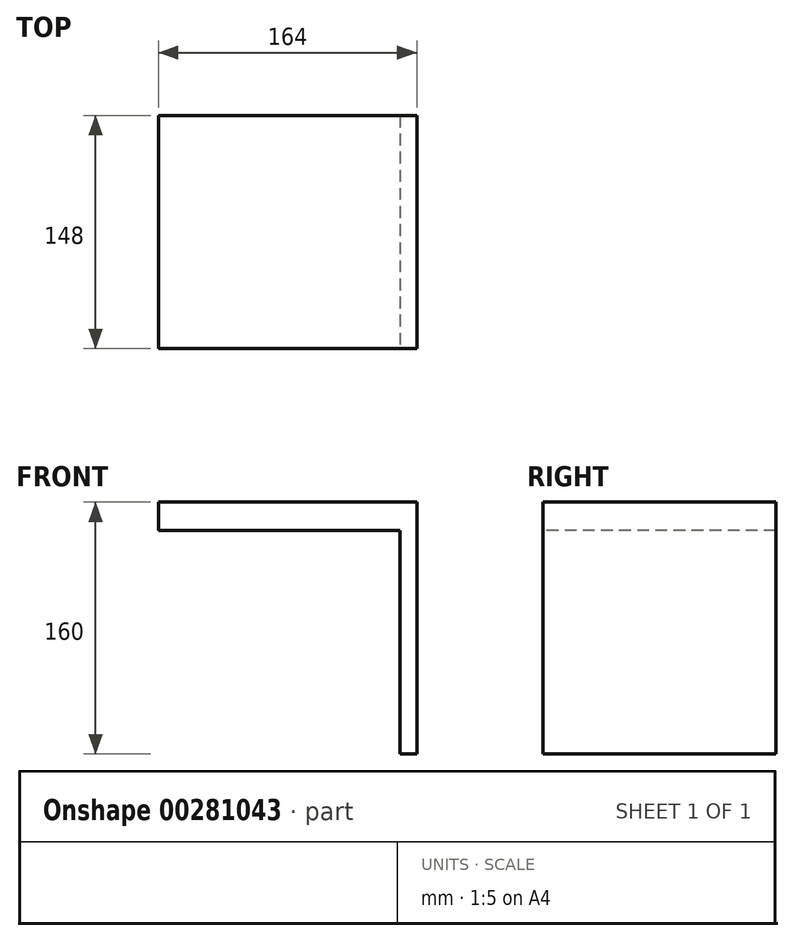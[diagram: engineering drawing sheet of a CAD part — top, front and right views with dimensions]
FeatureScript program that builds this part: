
annotation { "Feature Type Name" : "Feature", "Feature Type Description" : "" }
export const myFeature = defineFeature(function(context is Context, id is Id, definition is map)
    precondition{}
    {
        {
            var Q0;
            Q0=qCreatedBy(makeId("Front.planeOp"),FACE);
            var sketch = newSketch(context, id + "F0", { "sketchPlane" : qUnion([Q0])});
            skLineSegment(sketch, "E0.bottom", {"start": v(-41.99, 130) * mm, "end": v(135.01, 130) * mm});
            skLineSegment(sketch, "E0.top", {"start": v(-41.99, -47) * mm, "end": v(135.01, -47) * mm});
            skLineSegment(sketch, "E0.left", {"start": v(-41.99, 130) * mm, "end": v(-41.99, -47) * mm});
            skLineSegment(sketch, "E0.right", {"start": v(135.01, 130) * mm, "end": v(135.01, -47) * mm});
            skLineSegment(sketch, "E1.bottom", {"start": v(-29.69, 65.72) * mm, "end": v(134.31, 65.72) * mm});
            skLineSegment(sketch, "E1.top", {"start": v(-29.69, -23.24) * mm, "end": v(134.31, -23.24) * mm});
            skLineSegment(sketch, "E1.left", {"start": v(-29.69, 65.72) * mm, "end": v(-29.69, -23.24) * mm});
            skLineSegment(sketch, "E1.right", {"start": v(134.31, 65.72) * mm, "end": v(134.31, -23.24) * mm});
            skLineSegment(sketch, "E2.bottom", {"start": v(-18.19, 148.02) * mm, "end": v(145.81, 148.02) * mm});
            skLineSegment(sketch, "E2.top", {"start": v(-18.19, -11.98) * mm, "end": v(145.81, -11.98) * mm});
            skLineSegment(sketch, "E2.left", {"start": v(-18.19, 148.02) * mm, "end": v(-18.19, -11.98) * mm});
            skLineSegment(sketch, "E2.right", {"start": v(145.81, 148.02) * mm, "end": v(145.81, -11.98) * mm});
            skLineSegment(sketch, "E3", {"start": v(-41.99, 130) * mm, "end": v(-29.69, 65.72) * mm});
            skLineSegment(sketch, "E4", {"start": v(135.01, 130) * mm, "end": v(134.31, 65.72) * mm});
            skLineSegment(sketch, "E5", {"start": v(-41.99, -47) * mm, "end": v(-29.69, -23.24) * mm});
            skLineSegment(sketch, "E6", {"start": v(135.01, -47) * mm, "end": v(134.31, -23.24) * mm});
            skLineSegment(sketch, "E7", {"start": v(145.81, -11.98) * mm, "end": v(134.31, -23.24) * mm});
            skLineSegment(sketch, "E8", {"start": v(134.31, 65.72) * mm, "end": v(145.81, 148.02) * mm});
            skLineSegment(sketch, "E9", {"start": v(-29.69, 65.72) * mm, "end": v(-18.19, 148.02) * mm});
            skLineSegment(sketch, "E10", {"start": v(-29.69, -23.24) * mm, "end": v(-18.19, -11.98) * mm});
            skSolve(sketch);
        }
        {
            var Q0;
            {var subQ5=sQuery(id+"F0.wireOp",EDGE,"E2.right");Q0=makeQuery(id+"F0.imprint","IMPRINT",FACE,{"disambiguationData":[TD([[makeQuery(id+"F0.imprint","IMPRINT",EDGE,{"derivedFrom":subQ5}),-1.0]])]});}
            var Q1;
            {var subQ0=sQuery(id+"F0.wireOp",EDGE,"E2.bottom");Q1=makeQuery(id+"F0.imprint","IMPRINT",FACE,{"disambiguationData":[TD([[makeQuery(id+"F0.imprint","IMPRINT",EDGE,{"derivedFrom":subQ0}),-1.0]])]});}
            extrude(context, id + "F1", {"entities" : qUnion([Q0, Q1]), "oppositeDirection" : true, "depth" : 148 * mm});
        }
    });
